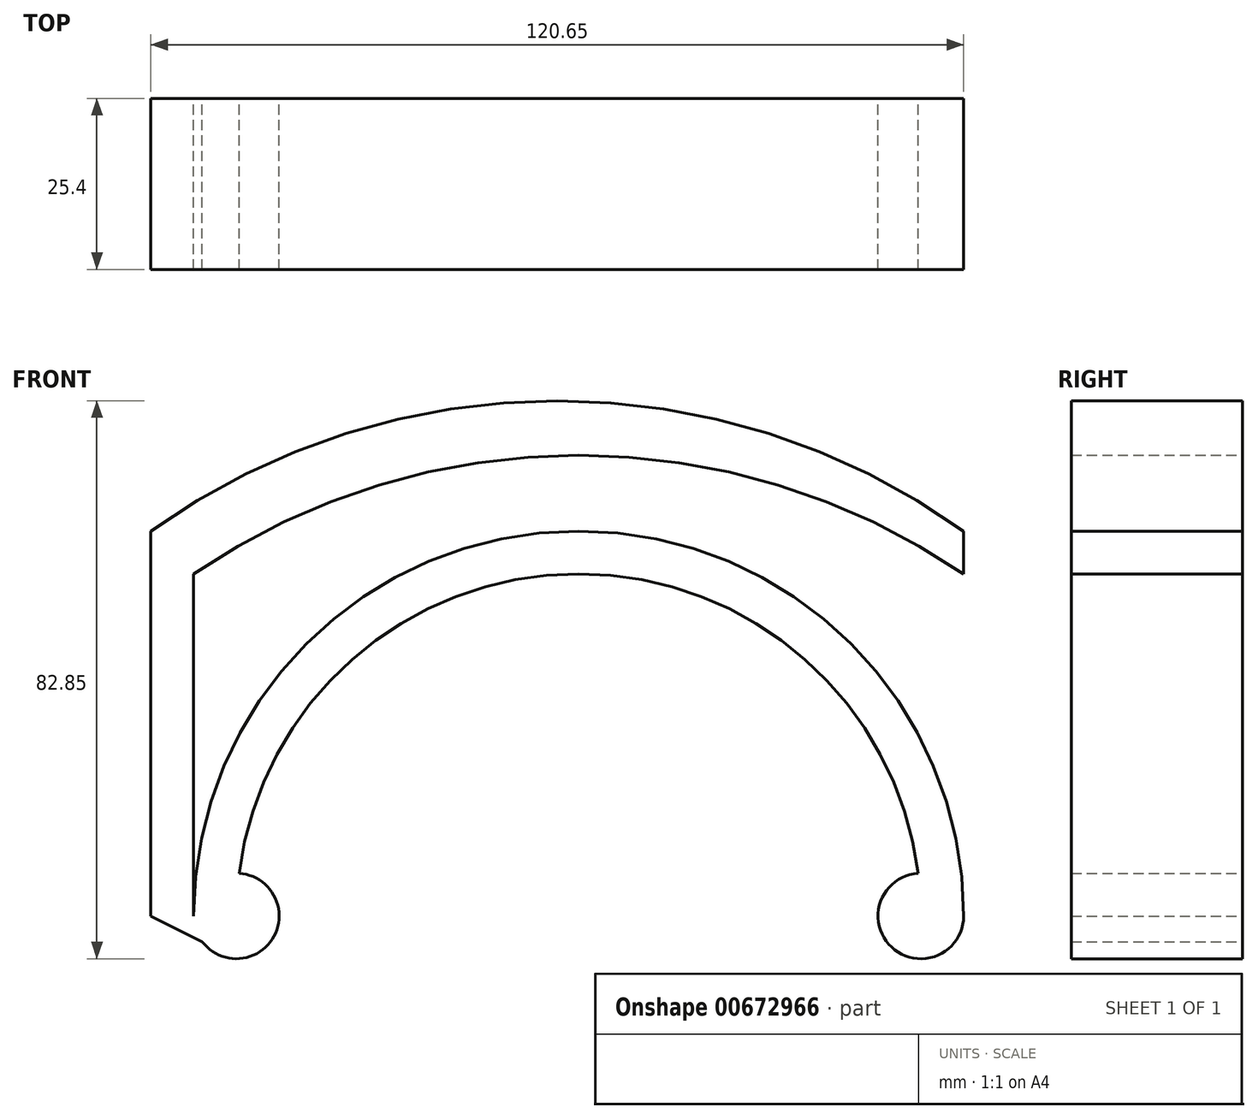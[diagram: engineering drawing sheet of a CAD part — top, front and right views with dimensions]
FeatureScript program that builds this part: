
annotation { "Feature Type Name" : "Feature", "Feature Type Description" : "" }
export const myFeature = defineFeature(function(context is Context, id is Id, definition is map)
    precondition{}
    {
        {
            var Q0;
            Q0=qCreatedBy(makeId("Front.planeOp"),FACE);
            var sketch = newSketch(context, id + "F0", { "sketchPlane" : qUnion([Q0])});
            skLineSegment(sketch, "E0", {"start": v(0, 0) * mm, "end": v(-50.8, 0) * mm});
            skLineSegment(sketch, "E1", {"start": v(0, 0) * mm, "end": v(50.8, 0) * mm});
            skArc(sketch, "E2", {"start": v(50.8, 0) * mm, "mid": v(0, 50.8) * mm, "end": v(-50.8, 0) * mm});
            skCircle(sketch, "E3", {"center": v(-50.8, 0) * mm, "radius": 6.35 * mm});
            skCircle(sketch, "E4", {"center": v(50.8, 0) * mm, "radius": 6.35 * mm});
            skArc(sketch, "E5", {"start": v(57.15, 0) * mm, "mid": v(0, 57.15) * mm, "end": v(-57.15, 0) * mm});
            skLineSegment(sketch, "E6", {"start": v(-57.15, 0) * mm, "end": v(-57.15, 50.8) * mm});
            skArc(sketch, "E7", {"start": v(57.15, 50.8) * mm, "mid": v(0, 68.4) * mm, "end": v(-57.15, 50.8) * mm});
            skLineSegment(sketch, "E8", {"start": v(-57.15, 0) * mm, "end": v(-63.5, 0) * mm});
            skLineSegment(sketch, "E9", {"start": v(-63.5, 0) * mm, "end": v(-63.5, 57.15) * mm});
            skLineSegment(sketch, "E10", {"start": v(57.15, 50.8) * mm, "end": v(57.15, 57.15) * mm});
            skArc(sketch, "E11", {"start": v(57.15, 57.15) * mm, "mid": v(-3.17, 76.5) * mm, "end": v(-63.5, 57.15) * mm});
            skLineSegment(sketch, "E12", {"start": v(-63.5, 0) * mm, "end": v(-50.8, -6.35) * mm});
            skSolve(sketch);
        }
        {
            var Q0;
            Q0=makeQuery(id+"F0.imprint","IMPRINT",FACE,{"disambiguationData":[TD([[makeQuery(id+"F0.imprint","IMPRINT",EDGE,{"derivedFrom":sQuery(id+"F0.wireOp",EDGE,"E6")}),1.0]])]});
            var Q1;
            {var subQ0=sQuery(id+"F0.wireOp",EDGE,"E2");var subQ1=sQuery(id+"F0.wireOp",EDGE,"E0");var subQ2=makeQuery(id+"F0.imprint","INTERSECT",VERTEX,{"derivedFrom":[subQ1,subQ0]});Q1=makeQuery(id+"F0.imprint","IMPRINT",FACE,{"disambiguationData":[TD([[makeQuery(id+"F0.imprint","IMPRINT",EDGE,{"disambiguationData":[TD([[subQ2,1.0]])],"derivedFrom":subQ1}),1.0]])]});}
            var Q2;
            {var subQ5=sQuery(id+"F0.wireOp",EDGE,"E5");Q2=makeQuery(id+"F0.imprint","IMPRINT",FACE,{"disambiguationData":[TD([[makeQuery(id+"F0.imprint","IMPRINT",EDGE,{"derivedFrom":subQ5}),1.0]])]});}
            var Q3;
            {var subQ0=sQuery(id+"F0.wireOp",EDGE,"E2");var subQ1=sQuery(id+"F0.wireOp",EDGE,"E0");var subQ2=makeQuery(id+"F0.imprint","INTERSECT",VERTEX,{"derivedFrom":[subQ1,subQ0]});Q3=makeQuery(id+"F0.imprint","IMPRINT",FACE,{"disambiguationData":[TD([[makeQuery(id+"F0.imprint","IMPRINT",EDGE,{"disambiguationData":[TD([[subQ2,1.0]])],"derivedFrom":subQ1}),-1.0]])]});}
            var Q4;
            {var subQ0=sQuery(id+"F0.wireOp",EDGE,"E2");var subQ1=sQuery(id+"F0.wireOp",EDGE,"E1");var subQ2=makeQuery(id+"F0.imprint","INTERSECT",VERTEX,{"derivedFrom":[subQ1,subQ0]});Q4=makeQuery(id+"F0.imprint","IMPRINT",FACE,{"disambiguationData":[TD([[makeQuery(id+"F0.imprint","IMPRINT",EDGE,{"disambiguationData":[TD([[subQ2,1.0]])],"derivedFrom":subQ1}),1.0]])]});}
            var Q5;
            {var subQ0=sQuery(id+"F0.wireOp",EDGE,"E2");var subQ1=sQuery(id+"F0.wireOp",EDGE,"E1");var subQ2=makeQuery(id+"F0.imprint","INTERSECT",VERTEX,{"derivedFrom":[subQ1,subQ0]});Q5=makeQuery(id+"F0.imprint","IMPRINT",FACE,{"disambiguationData":[TD([[makeQuery(id+"F0.imprint","IMPRINT",EDGE,{"disambiguationData":[TD([[subQ2,1.0]])],"derivedFrom":subQ1}),-1.0]])]});}
            var Q6;
            {var subQ0=sQuery(id+"F0.wireOp",EDGE,"E8");Q6=makeQuery(id+"F0.imprint","IMPRINT",FACE,{"disambiguationData":[TD([[makeQuery(id+"F0.imprint","IMPRINT",EDGE,{"derivedFrom":subQ0}),1.0]])]});}
            var Q7;
            {var subQ0=sQuery(id+"F0.wireOp",EDGE,"E12");var subQ1=sQuery(id+"F0.wireOp",EDGE,"E3");var subQ2=makeQuery(id+"F0.imprint","INTERSECT",VERTEX,{"disambiguationData":[OD(0.0)],"derivedFrom":[subQ1,subQ0]});Q7=makeQuery(id+"F0.imprint","IMPRINT",FACE,{"disambiguationData":[TD([[makeQuery(id+"F0.imprint","IMPRINT",EDGE,{"disambiguationData":[TD([[subQ2,1.0]])],"derivedFrom":subQ1}),1.0]])]});}
            extrude(context, id + "F1", {"entities" : qUnion([Q0, Q1, Q2, Q3, Q4, Q5, Q6, Q7]), "depth" : 25.4 * mm, "offsetDistance" : 25.4 * mm});
        }
    });
